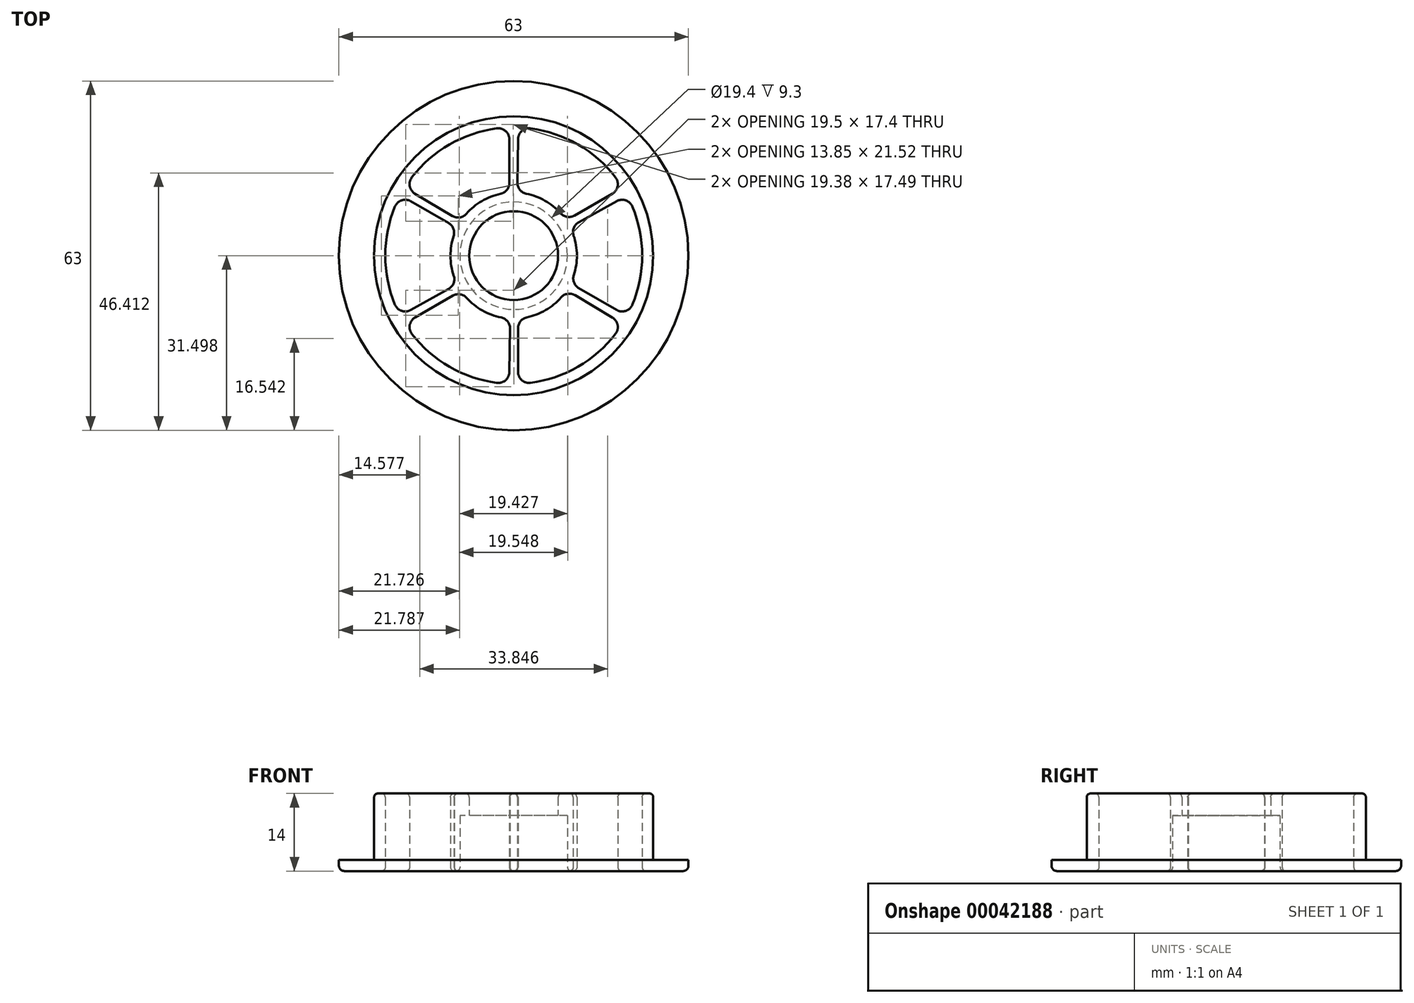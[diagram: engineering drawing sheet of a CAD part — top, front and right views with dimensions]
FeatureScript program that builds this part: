
annotation { "Feature Type Name" : "Feature", "Feature Type Description" : "" }
export const myFeature = defineFeature(function(context is Context, id is Id, definition is map)
    precondition{}
    {
        {
            var Q0;
            Q0=qCreatedBy(makeId("Top.planeOp"),FACE);
            var sketch = newSketch(context, id + "F0", { "sketchPlane" : qUnion([Q0])});
            skCircle(sketch, "E0", {"center": v(0, 0) * mm, "radius": 9.7 * mm});
            skCircle(sketch, "E1", {"center": v(0, 0) * mm, "radius": 8 * mm});
            skCircle(sketch, "E2", {"center": v(0, 0) * mm, "radius": 25.15 * mm});
            skCircle(sketch, "E3", {"center": v(0, 0) * mm, "radius": 31.5 * mm});
            skLineSegment(sketch, "E4.0", {"start": v(0.78, -13.1) * mm, "end": v(0.78, -20.97) * mm});
            skLineSegment(sketch, "E4.1", {"start": v(11.06, -7.15) * mm, "end": v(17.8, -11.18) * mm});
            skArc(sketch, "E5", {"start": v(3.05, -22.95) * mm, "mid": v(11.58, -20.05) * mm, "end": v(18.35, -14.11) * mm});
            skArc(sketch, "E6", {"start": v(2.37, -11.14) * mm, "mid": v(5.74, -9.84) * mm, "end": v(8.53, -7.54) * mm});
            skArc(sketch, "E7.filletArc", {"start": v(0.78, -20.97) * mm, "mid": v(1.47, -22.47) * mm, "end": v(3.05, -22.95) * mm});
            skArc(sketch, "E8.filletArc", {"start": v(18.35, -14.11) * mm, "mid": v(18.73, -12.52) * mm, "end": v(17.8, -11.18) * mm});
            skArc(sketch, "E9.filletArc", {"start": v(11.06, -7.15) * mm, "mid": v(9.73, -6.89) * mm, "end": v(8.53, -7.54) * mm});
            skArc(sketch, "E10.filletArc", {"start": v(2.37, -11.14) * mm, "mid": v(1.23, -11.84) * mm, "end": v(0.78, -13.1) * mm});
            skArc(sketch, "E11.1.0", {"start": v(18.55, -9.8) * mm, "mid": v(20.2, -9.97) * mm, "end": v(21.4, -8.84) * mm});
            skLineSegment(sketch, "E11.1.1", {"start": v(11.73, -5.87) * mm, "end": v(18.55, -9.8) * mm});
            skArc(sketch, "E11.1.2", {"start": v(10.83, -3.52) * mm, "mid": v(11.39, 0.05) * mm, "end": v(10.8, 3.62) * mm});
            skArc(sketch, "E11.1.3", {"start": v(10.83, -3.52) * mm, "mid": v(10.87, -4.86) * mm, "end": v(11.73, -5.87) * mm});
            skLineSegment(sketch, "E11.1.4", {"start": v(11.72, 6) * mm, "end": v(18.58, 9.82) * mm});
            skArc(sketch, "E11.1.5", {"start": v(21.4, -8.84) * mm, "mid": v(23.15, 0) * mm, "end": v(21.4, 8.84) * mm});
            skArc(sketch, "E11.1.6", {"start": v(21.4, 8.84) * mm, "mid": v(20.2, 9.96) * mm, "end": v(18.58, 9.82) * mm});
            skArc(sketch, "E11.1.7", {"start": v(11.72, 6) * mm, "mid": v(10.83, 4.98) * mm, "end": v(10.8, 3.62) * mm});
            skArc(sketch, "E11.2.0", {"start": v(17.77, 11.16) * mm, "mid": v(18.73, 12.5) * mm, "end": v(18.35, 14.11) * mm});
            skLineSegment(sketch, "E11.2.1", {"start": v(10.95, 7.23) * mm, "end": v(17.77, 11.16) * mm});
            skArc(sketch, "E11.2.2", {"start": v(8.46, 7.62) * mm, "mid": v(5.65, 9.89) * mm, "end": v(2.26, 11.16) * mm});
            skArc(sketch, "E11.2.3", {"start": v(8.46, 7.62) * mm, "mid": v(9.64, 6.98) * mm, "end": v(10.95, 7.23) * mm});
            skLineSegment(sketch, "E11.2.4", {"start": v(0.66, 13.15) * mm, "end": v(0.78, 21) * mm});
            skArc(sketch, "E11.2.5", {"start": v(18.35, 14.11) * mm, "mid": v(11.57, 20.05) * mm, "end": v(3.05, 22.95) * mm});
            skArc(sketch, "E11.2.6", {"start": v(3.05, 22.95) * mm, "mid": v(1.48, 22.48) * mm, "end": v(0.78, 21) * mm});
            skArc(sketch, "E11.2.7", {"start": v(0.66, 13.15) * mm, "mid": v(1.1, 11.87) * mm, "end": v(2.26, 11.16) * mm});
            skArc(sketch, "E11.3.0", {"start": v(-0.78, 20.97) * mm, "mid": v(-1.47, 22.47) * mm, "end": v(-3.05, 22.95) * mm});
            skLineSegment(sketch, "E11.3.1", {"start": v(-0.78, 13.1) * mm, "end": v(-0.78, 20.97) * mm});
            skArc(sketch, "E11.3.2", {"start": v(-2.37, 11.14) * mm, "mid": v(-5.74, 9.84) * mm, "end": v(-8.53, 7.54) * mm});
            skArc(sketch, "E11.3.3", {"start": v(-2.37, 11.14) * mm, "mid": v(-1.23, 11.84) * mm, "end": v(-0.78, 13.1) * mm});
            skLineSegment(sketch, "E11.3.4", {"start": v(-11.06, 7.15) * mm, "end": v(-17.8, 11.18) * mm});
            skArc(sketch, "E11.3.5", {"start": v(-3.05, 22.95) * mm, "mid": v(-11.57, 20.05) * mm, "end": v(-18.35, 14.11) * mm});
            skArc(sketch, "E11.3.6", {"start": v(-18.35, 14.11) * mm, "mid": v(-18.73, 12.52) * mm, "end": v(-17.8, 11.18) * mm});
            skArc(sketch, "E11.3.7", {"start": v(-11.06, 7.15) * mm, "mid": v(-9.73, 6.89) * mm, "end": v(-8.53, 7.54) * mm});
            skArc(sketch, "E11.4.0", {"start": v(-18.55, 9.8) * mm, "mid": v(-20.2, 9.97) * mm, "end": v(-21.4, 8.84) * mm});
            skLineSegment(sketch, "E11.4.1", {"start": v(-11.73, 5.87) * mm, "end": v(-18.55, 9.8) * mm});
            skArc(sketch, "E11.4.2", {"start": v(-10.83, 3.52) * mm, "mid": v(-11.39, -0.05) * mm, "end": v(-10.8, -3.62) * mm});
            skArc(sketch, "E11.4.3", {"start": v(-10.83, 3.52) * mm, "mid": v(-10.87, 4.86) * mm, "end": v(-11.73, 5.87) * mm});
            skLineSegment(sketch, "E11.4.4", {"start": v(-11.72, -6) * mm, "end": v(-18.58, -9.82) * mm});
            skArc(sketch, "E11.4.5", {"start": v(-21.4, 8.84) * mm, "mid": v(-23.15, 0) * mm, "end": v(-21.4, -8.84) * mm});
            skArc(sketch, "E11.4.6", {"start": v(-21.4, -8.84) * mm, "mid": v(-20.2, -9.96) * mm, "end": v(-18.58, -9.82) * mm});
            skArc(sketch, "E11.4.7", {"start": v(-11.72, -6) * mm, "mid": v(-10.83, -4.98) * mm, "end": v(-10.8, -3.62) * mm});
            skArc(sketch, "E11.5.0", {"start": v(-17.77, -11.16) * mm, "mid": v(-18.73, -12.5) * mm, "end": v(-18.35, -14.11) * mm});
            skLineSegment(sketch, "E11.5.1", {"start": v(-10.95, -7.23) * mm, "end": v(-17.77, -11.16) * mm});
            skArc(sketch, "E11.5.2", {"start": v(-8.46, -7.62) * mm, "mid": v(-5.65, -9.89) * mm, "end": v(-2.26, -11.16) * mm});
            skArc(sketch, "E11.5.3", {"start": v(-8.46, -7.62) * mm, "mid": v(-9.64, -6.98) * mm, "end": v(-10.95, -7.23) * mm});
            skLineSegment(sketch, "E11.5.4", {"start": v(-0.66, -13.15) * mm, "end": v(-0.78, -21) * mm});
            skArc(sketch, "E11.5.5", {"start": v(-18.35, -14.11) * mm, "mid": v(-11.57, -20.05) * mm, "end": v(-3.05, -22.95) * mm});
            skArc(sketch, "E11.5.6", {"start": v(-3.05, -22.95) * mm, "mid": v(-1.48, -22.48) * mm, "end": v(-0.78, -21) * mm});
            skArc(sketch, "E11.5.7", {"start": v(-0.66, -13.15) * mm, "mid": v(-1.1, -11.87) * mm, "end": v(-2.26, -11.16) * mm});
            skSolve(sketch);
        }
        {
            var Q0;
            Q0 = qSketchRegion(id + "F0", true);
            extrude(context, id + "F1", {"entities" : qUnion([Q0]), "depth" : 2 * mm});
        }
        {
            var Q0;
            Q0=makeQuery(id+"F0.imprint","IMPRINT",FACE,{"disambiguationData":[TD([[makeQuery(id+"F0.imprint","IMPRINT",EDGE,{"derivedFrom":sQuery(id+"F0.wireOp",EDGE,"E0")}),-1.0]])]});
            extrude(context, id + "F2", {"entities" : qUnion([Q0]), "operationType" : NewBodyOperationType.ADD, "depth" : 14 * mm});
        }
        {
            var Q0;
            Q0=makeQuery(id+"F0.imprint","IMPRINT",FACE,{"disambiguationData":[TD([[makeQuery(id+"F0.imprint","IMPRINT",EDGE,{"derivedFrom":sQuery(id+"F0.wireOp",EDGE,"E0")}),1.0]])]});
            extrude(context, id + "F3", {"entities" : qUnion([Q0]), "operationType" : NewBodyOperationType.ADD, "depth" : 14 * mm});
        }
        {
            var Q0;
            Q0=makeQuery(id+"F0.imprint","IMPRINT",FACE,{"disambiguationData":[TD([[makeQuery(id+"F0.imprint","IMPRINT",EDGE,{"derivedFrom":sQuery(id+"F0.wireOp",EDGE,"E0")}),1.0]])]});
            extrude(context, id + "F4", {"entities" : qUnion([Q0]), "operationType" : NewBodyOperationType.REMOVE, "depth" : 10 * mm});
        }
        {
            var Q0;
            Q0=makeQuery(id+"F1.opExtrude","CAP_EDGE",EDGE,{"disambiguationData":[OSD([sQuery(id+"F0.wireOp",EDGE,"E3")])],"isStart":true});
            fillet(context, id + "F5", {"entities" : qUnion([Q0]), "radius" : 1 * mm, "tangentPropagation" : true, "allowEdgeOverflow" : false});
        }
        {
            var Q0;
            {var subQ0=sQuery(id+"F0.wireOp",EDGE,"E0");Q0=makeQuery(id+"F3.boolean.opBoolean","MERGE",FACE,{"derivedFrom":[makeQuery(id+"F2.opExtrude","CAP_FACE",FACE,{"disambiguationData":[OSD([subQ0,sQuery(id+"F0.wireOp",EDGE,"E2"),sQuery(id+"F0.wireOp",EDGE,"E4.0"),sQuery(id+"F0.wireOp",EDGE,"E4.1"),sQuery(id+"F0.wireOp",EDGE,"E5"),sQuery(id+"F0.wireOp",EDGE,"E6"),sQuery(id+"F0.wireOp",EDGE,"E7.filletArc"),sQuery(id+"F0.wireOp",EDGE,"E8.filletArc"),sQuery(id+"F0.wireOp",EDGE,"E9.filletArc"),sQuery(id+"F0.wireOp",EDGE,"E10.filletArc"),sQuery(id+"F0.wireOp",EDGE,"E11.1.0"),sQuery(id+"F0.wireOp",EDGE,"E11.1.1"),sQuery(id+"F0.wireOp",EDGE,"E11.1.2"),sQuery(id+"F0.wireOp",EDGE,"E11.1.3"),sQuery(id+"F0.wireOp",EDGE,"E11.1.4"),sQuery(id+"F0.wireOp",EDGE,"E11.1.5"),sQuery(id+"F0.wireOp",EDGE,"E11.1.6"),sQuery(id+"F0.wireOp",EDGE,"E11.1.7"),sQuery(id+"F0.wireOp",EDGE,"E11.2.0"),sQuery(id+"F0.wireOp",EDGE,"E11.2.1"),sQuery(id+"F0.wireOp",EDGE,"E11.2.2"),sQuery(id+"F0.wireOp",EDGE,"E11.2.3"),sQuery(id+"F0.wireOp",EDGE,"E11.2.4"),sQuery(id+"F0.wireOp",EDGE,"E11.2.5"),sQuery(id+"F0.wireOp",EDGE,"E11.2.6"),sQuery(id+"F0.wireOp",EDGE,"E11.2.7"),sQuery(id+"F0.wireOp",EDGE,"E11.3.0"),sQuery(id+"F0.wireOp",EDGE,"E11.3.1"),sQuery(id+"F0.wireOp",EDGE,"E11.3.2"),sQuery(id+"F0.wireOp",EDGE,"E11.3.3"),sQuery(id+"F0.wireOp",EDGE,"E11.3.4"),sQuery(id+"F0.wireOp",EDGE,"E11.3.5"),sQuery(id+"F0.wireOp",EDGE,"E11.3.6"),sQuery(id+"F0.wireOp",EDGE,"E11.3.7"),sQuery(id+"F0.wireOp",EDGE,"E11.4.0"),sQuery(id+"F0.wireOp",EDGE,"E11.4.1"),sQuery(id+"F0.wireOp",EDGE,"E11.4.2"),sQuery(id+"F0.wireOp",EDGE,"E11.4.3"),sQuery(id+"F0.wireOp",EDGE,"E11.4.4"),sQuery(id+"F0.wireOp",EDGE,"E11.4.5"),sQuery(id+"F0.wireOp",EDGE,"E11.4.6"),sQuery(id+"F0.wireOp",EDGE,"E11.4.7"),sQuery(id+"F0.wireOp",EDGE,"E11.5.0"),sQuery(id+"F0.wireOp",EDGE,"E11.5.1"),sQuery(id+"F0.wireOp",EDGE,"E11.5.2"),sQuery(id+"F0.wireOp",EDGE,"E11.5.3"),sQuery(id+"F0.wireOp",EDGE,"E11.5.4"),sQuery(id+"F0.wireOp",EDGE,"E11.5.5"),sQuery(id+"F0.wireOp",EDGE,"E11.5.6"),sQuery(id+"F0.wireOp",EDGE,"E11.5.7")])],"isStart":false}),makeQuery(id+"F3.opExtrude","CAP_FACE",FACE,{"disambiguationData":[OSD([subQ0,sQuery(id+"F0.wireOp",EDGE,"E1")])],"isStart":false})]});}
            var Q1;
            {var subQ0=sQuery(id+"F0.wireOp",EDGE,"E0");var subQ1=sQuery(id+"F0.wireOp",EDGE,"E2");Q1=makeQuery(id+"F3.boolean.opBoolean","MERGE",FACE,{"derivedFrom":[makeQuery(id+"F2.boolean.opBoolean","MERGE",FACE,{"derivedFrom":[makeQuery(id+"F1.opExtrude","CAP_FACE",FACE,{"disambiguationData":[OSD([subQ1,sQuery(id+"F0.wireOp",EDGE,"E3")])],"isStart":true}),makeQuery(id+"F2.opExtrude","CAP_FACE",FACE,{"disambiguationData":[OSD([subQ0,subQ1,sQuery(id+"F0.wireOp",EDGE,"E4.0"),sQuery(id+"F0.wireOp",EDGE,"E4.1"),sQuery(id+"F0.wireOp",EDGE,"E5"),sQuery(id+"F0.wireOp",EDGE,"E6"),sQuery(id+"F0.wireOp",EDGE,"E7.filletArc"),sQuery(id+"F0.wireOp",EDGE,"E8.filletArc"),sQuery(id+"F0.wireOp",EDGE,"E9.filletArc"),sQuery(id+"F0.wireOp",EDGE,"E10.filletArc"),sQuery(id+"F0.wireOp",EDGE,"E11.1.0"),sQuery(id+"F0.wireOp",EDGE,"E11.1.1"),sQuery(id+"F0.wireOp",EDGE,"E11.1.2"),sQuery(id+"F0.wireOp",EDGE,"E11.1.3"),sQuery(id+"F0.wireOp",EDGE,"E11.1.4"),sQuery(id+"F0.wireOp",EDGE,"E11.1.5"),sQuery(id+"F0.wireOp",EDGE,"E11.1.6"),sQuery(id+"F0.wireOp",EDGE,"E11.1.7"),sQuery(id+"F0.wireOp",EDGE,"E11.2.0"),sQuery(id+"F0.wireOp",EDGE,"E11.2.1"),sQuery(id+"F0.wireOp",EDGE,"E11.2.2"),sQuery(id+"F0.wireOp",EDGE,"E11.2.3"),sQuery(id+"F0.wireOp",EDGE,"E11.2.4"),sQuery(id+"F0.wireOp",EDGE,"E11.2.5"),sQuery(id+"F0.wireOp",EDGE,"E11.2.6"),sQuery(id+"F0.wireOp",EDGE,"E11.2.7"),sQuery(id+"F0.wireOp",EDGE,"E11.3.0"),sQuery(id+"F0.wireOp",EDGE,"E11.3.1"),sQuery(id+"F0.wireOp",EDGE,"E11.3.2"),sQuery(id+"F0.wireOp",EDGE,"E11.3.3"),sQuery(id+"F0.wireOp",EDGE,"E11.3.4"),sQuery(id+"F0.wireOp",EDGE,"E11.3.5"),sQuery(id+"F0.wireOp",EDGE,"E11.3.6"),sQuery(id+"F0.wireOp",EDGE,"E11.3.7"),sQuery(id+"F0.wireOp",EDGE,"E11.4.0"),sQuery(id+"F0.wireOp",EDGE,"E11.4.1"),sQuery(id+"F0.wireOp",EDGE,"E11.4.2"),sQuery(id+"F0.wireOp",EDGE,"E11.4.3"),sQuery(id+"F0.wireOp",EDGE,"E11.4.4"),sQuery(id+"F0.wireOp",EDGE,"E11.4.5"),sQuery(id+"F0.wireOp",EDGE,"E11.4.6"),sQuery(id+"F0.wireOp",EDGE,"E11.4.7"),sQuery(id+"F0.wireOp",EDGE,"E11.5.0"),sQuery(id+"F0.wireOp",EDGE,"E11.5.1"),sQuery(id+"F0.wireOp",EDGE,"E11.5.2"),sQuery(id+"F0.wireOp",EDGE,"E11.5.3"),sQuery(id+"F0.wireOp",EDGE,"E11.5.4"),sQuery(id+"F0.wireOp",EDGE,"E11.5.5"),sQuery(id+"F0.wireOp",EDGE,"E11.5.6"),sQuery(id+"F0.wireOp",EDGE,"E11.5.7")])],"isStart":true})]}),makeQuery(id+"F3.opExtrude","CAP_FACE",FACE,{"disambiguationData":[OSD([subQ0,sQuery(id+"F0.wireOp",EDGE,"E1")])],"isStart":true})]});}
            fillet(context, id + "F6", {"entities" : qUnion([Q0, Q1]), "radius" : 0.7 * mm, "tangentPropagation" : true, "allowEdgeOverflow" : false});
        }
    });
